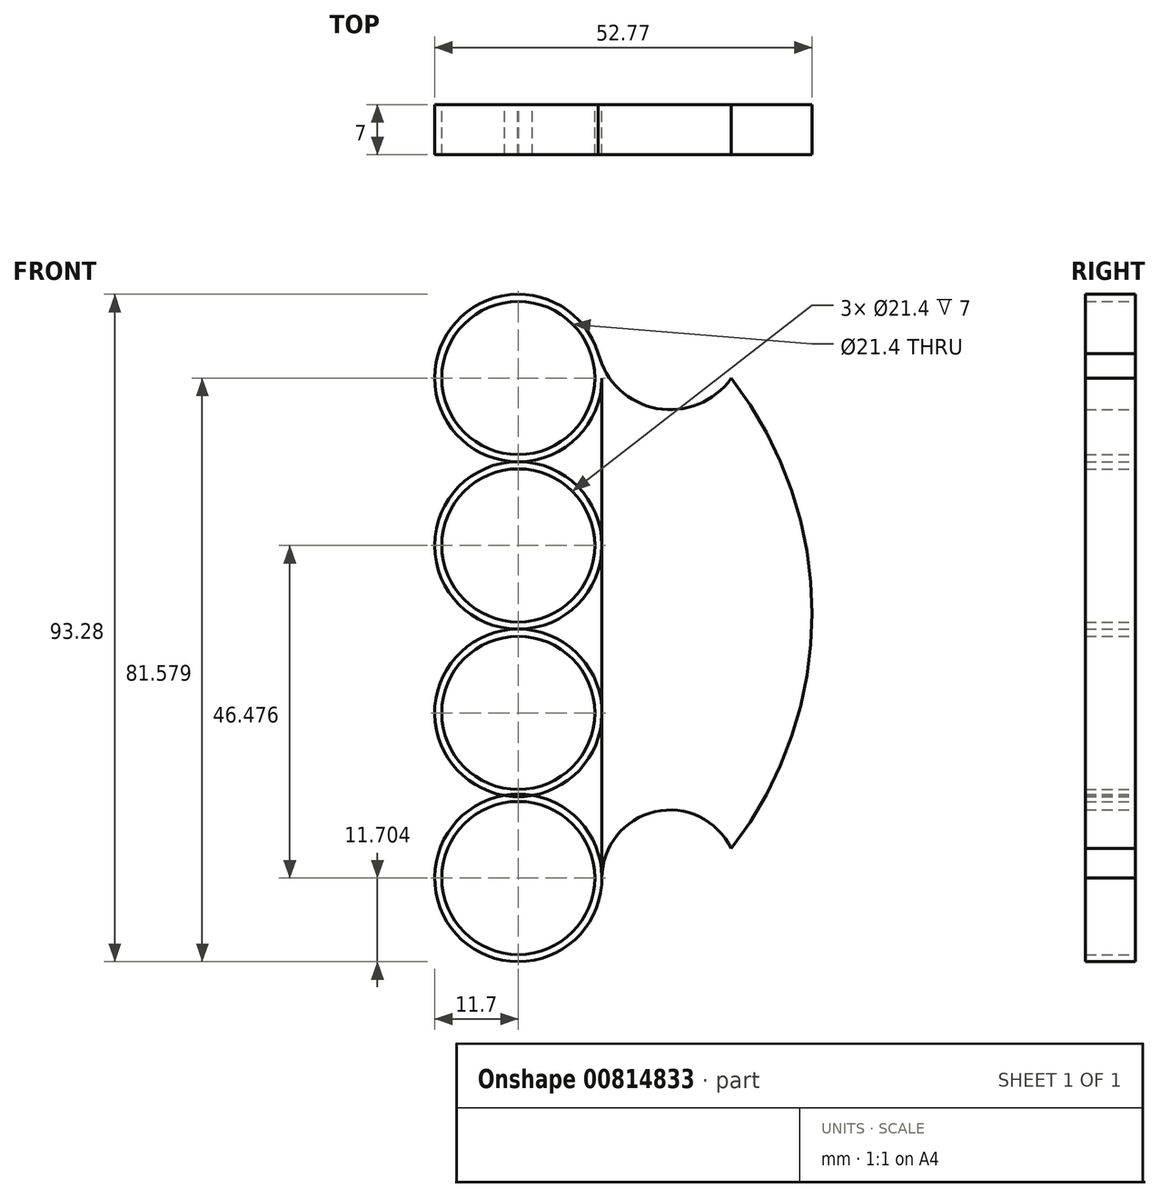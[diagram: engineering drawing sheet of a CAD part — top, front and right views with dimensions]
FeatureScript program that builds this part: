
annotation { "Feature Type Name" : "Feature", "Feature Type Description" : "" }
export const myFeature = defineFeature(function(context is Context, id is Id, definition is map)
    precondition{}
    {
        {
            var Q0;
            Q0=qCreatedBy(makeId("Front.planeOp"),FACE);
            var sketch = newSketch(context, id + "F0", { "sketchPlane" : qUnion([Q0])});
            skCircle(sketch, "E0", {"center": v(0, 0) * mm, "radius": 10.7 * mm});
            skCircle(sketch, "E1", {"center": v(0, 0) * mm, "radius": 11.7 * mm});
            skCircle(sketch, "E2", {"center": v(0, 23.4) * mm, "radius": 10.7 * mm});
            skCircle(sketch, "E3", {"center": v(0, 23.4) * mm, "radius": 11.7 * mm});
            skCircle(sketch, "E4.1.0", {"center": v(0, -23.4) * mm, "radius": 11.7 * mm});
            skCircle(sketch, "E4.1.1", {"center": v(0, -23.4) * mm, "radius": 10.7 * mm});
            skCircle(sketch, "E5", {"center": v(0, -46.48) * mm, "radius": 10.7 * mm});
            skCircle(sketch, "E6", {"center": v(0, -46.48) * mm, "radius": 11.7 * mm});
            skLineSegment(sketch, "E7", {"start": v(11.7, 23.4) * mm, "end": v(11.7, -46.48) * mm});
            skArc(sketch, "E8", {"start": v(29.77, -42.36) * mm, "mid": v(19.1, -37.21) * mm, "end": v(11.7, -46.48) * mm});
            skArc(sketch, "E9.MirrorCS", {"start": v(29.76, 23.36) * mm, "mid": v(19.36, 19.15) * mm, "end": v(11.19, 26.83) * mm});
            skArc(sketch, "E10", {"start": v(29.77, -42.36) * mm, "mid": v(41.07, -9.5) * mm, "end": v(29.76, 23.36) * mm});
            skPoint(sketch, "E11.end.orphan", {"position": v(12.78, 23.36) * mm});
            skSolve(sketch);
        }
        {
            var Q0;
            Q0=makeQuery(id+"F0.imprint","IMPRINT",FACE,{"disambiguationData":[TD([[makeQuery(id+"F0.imprint","IMPRINT",EDGE,{"derivedFrom":sQuery(id+"F0.wireOp",EDGE,"E2")}),-1.0]])]});
            var Q1;
            Q1=makeQuery(id+"F0.imprint","IMPRINT",FACE,{"disambiguationData":[TD([[makeQuery(id+"F0.imprint","IMPRINT",EDGE,{"derivedFrom":sQuery(id+"F0.wireOp",EDGE,"E0")}),-1.0]])]});
            var Q2;
            Q2=makeQuery(id+"F0.imprint","IMPRINT",FACE,{"disambiguationData":[TD([[makeQuery(id+"F0.imprint","IMPRINT",EDGE,{"derivedFrom":sQuery(id+"F0.wireOp",EDGE,"E4.1.1")}),-1.0]])]});
            var Q3;
            {var subQ0=sQuery(id+"F0.wireOp",EDGE,"E8");Q3=makeQuery(id+"F0.imprint","IMPRINT",FACE,{"disambiguationData":[TD([[makeQuery(id+"F0.imprint","IMPRINT",EDGE,{"derivedFrom":subQ0}),-1.0]])]});}
            var Q4;
            Q4=makeQuery(id+"F0.imprint","IMPRINT",FACE,{"disambiguationData":[TD([[makeQuery(id+"F0.imprint","IMPRINT",EDGE,{"derivedFrom":sQuery(id+"F0.wireOp",EDGE,"E5")}),-1.0]])]});
            extrude(context, id + "F1", {"entities" : qUnion([Q0, Q1, Q2, Q3, Q4]), "depth" : 7 * mm, "offsetDistance" : 25 * mm});
        }
    });
